# Revit family: BE_99115_de_DE
name_source: partatom
category: Leuchten
revit_build: Autodesk Revit 2015 (Build: 20160512_0715(x64)
units: mm (PartAtom-declared; Revit-internal decimal feet)

## types (1)
- BEGA_99115_K3
    AC/DC = DC
    Aktualisierung = 2017-03-06T04:16:18
    Anschlussleitung = 4.0 m 05RN8-F 2 × 1²
    BEGA_Dummy = Nein
    BEGA_IES1 = Ja
    BEGA_IES2 = Ja
    BEGA_IES3 = Ja
    BEGA_Intern = Ja
    BEGA_Intern_Konstruktion = Ja
    BEGA_Intern_an = Ja
    BEGA_Intern_aus = Ja
    Befestigungsbohrung = Ø 7 mm
    Beschreibung = Unterwasserscheinwerfer
    Beschreibung_Sonderanfertigung = Hier können Sie Informationen zur Sonderanfertigung eintragen.
    Bestellnummer = 99115
    CE_Konformität = ja
    Energieeffizienzklasse = LED A++ - A
    Farbtemperatur = 3000 K
    Farbwiedergabeindex = Ra > 80
    Gewicht = 1.1 kg
    Hersteller = BEGA
    LED_Modulbezeichnung = LED-0401/830
    Lampe = LED 16.9 W
    Lampenlichtstrom = 1965 lm
    Lastklassifizierung = Beleuchtung
    Lebensdauerkriterien = L70 = 50.000 h
    Leuchtenlichtstrom = 1150 lm
    Logo = BEGA_Logo.png
    M_A = Ja
    M_G = Ja
    M_W = Ja
    Material_02 = BEGA_Oberfläche_Silber_matt
    Material_03 = BEGA_Oberfläche_Weiss_matt
    Material_06 = BEGA_Oberfläche_Edelstahl_gebürstet
    Material_09 = BEGA_Glas_klar
    Material_11 = BEGA_Glas_opal
    Material_15 = BEGA_Leuchtmedium_matt
    Material_17 = BEGA_Reflektor
    Material_18 = BEGA_Gummi_schwarz
    Modell = 99115
    Produktdatenblatt = http://www.bega.de
    Scheinlast = 0 VA
    Schutzart = IP 68...20 m
    Schutzklasse = III
    Sonderanfertigung = Nein
    Spannung = 24 V
    Typenbild = 99115.png
    URL = http://www.bega.de
    Vorgabe-Ansicht = 0 mm  [stored 0 ft]

note: [stored X ft] marks values corroborated as IEEE doubles in the binary element streams (Revit-internal decimal feet)

## geometry (parser evidence)
native form markers: Blend x2, Sweep x11
no freeform markers — native parametric forms only
